# Revit family: Fireplace_Electric_HeatNGlo_SimpliFire-Wall
name_source: partatom
category: Generic Models
revit_build: Autodesk Revit 2015 (Build: 20140323_1530(x64)
units: mm (PartAtom-declared; Revit-internal decimal feet)

## types (4) — shared parameters
Assembly Code = D3020
Construction Details = http://www.arcat.com
Default Elevation = 0' - 0"
Electrical_Amperage = 13 A
Electrical_Frequency = 60 Hz
Electrical_Phase = 1
Electrical_Voltage = 120 V
Electrical_Wattage = 1500 W
HVAC_BTU Output = 4800.0 Btu/h
Keynote = 10305
Manufacturer = Heat & Glo
Manufacturer Website = http://www.heatnglo.com
Product Data = http://www.arcat.com
Revision = R1_2014-11
Sales Information = http://www.heatnglo.com
Send Message = http://www.arcat.com
Specification = http://www.arcat.com
Standards Conformance = CSA
URL = http://www.heatnglo.com
zero-valued in all types: Expected Lifespan (Years), Maintenance Schedule (Months), Unit Weight, Warranty Duration (Years)

## per-type parameters (varying)
| type | Description | Model | Offset from Top | Offset from Wall | Opening Height | Opening Width | Rear Height | Rear Width | Unit Height | Unit Width |
| 75x11 Viewing Area | Heat & Glo Electric Fireplace - SimpliFire SF-WM94 as Specified | SF-WM94 | 0' - 7 11/16" | 0' - 6" | 0' - 11" | 6' - 2 13/16" | 1' - 8 1/4" | 6' - 6 3/8" | 2' - 2 3/8" | 7' - 9 3/4" |
| 51x11 Viewing Area | Heat & Glo Electric Fireplace - SimpliFire SF-WM70 as Specified | SF-WM70 | 0' - 7 11/16" | 0' - 6" | 0' - 11" | 4' - 3 3/16" | 1' - 8 1/4" | 4' - 6 3/4" | 2' - 2 3/8" | 5' - 10 3/32" |
| 40x11 Viewing Area | Heat & Glo Electric Fireplace - SimpliFire SF-WM58 as Specified | SF-WM58 | 0' - 7 11/16" | 0' - 6" | 0' - 11" | 3' - 3 3/8" | 1' - 8 1/4" | 3' - 6 15/16" | 2' - 2 3/8" | 4' - 10 1/4" |
| 29x9 Viewing Area | Heat & Glo Electric Fireplace - SimpliFire SF-WM38 as Specified | SF-WM38 | 0' - 3 15/16" | 0' - 4 7/8" | 0' - 8 1/4" | 2' - 4 3/8" | 1' - 1 5/8" | 2' - 8 1/4" | 1' - 4 15/16" | 3' - 1 13/16" |

## geometry (parser evidence)
native form markers: Sweep x3
no freeform markers — native parametric forms only
